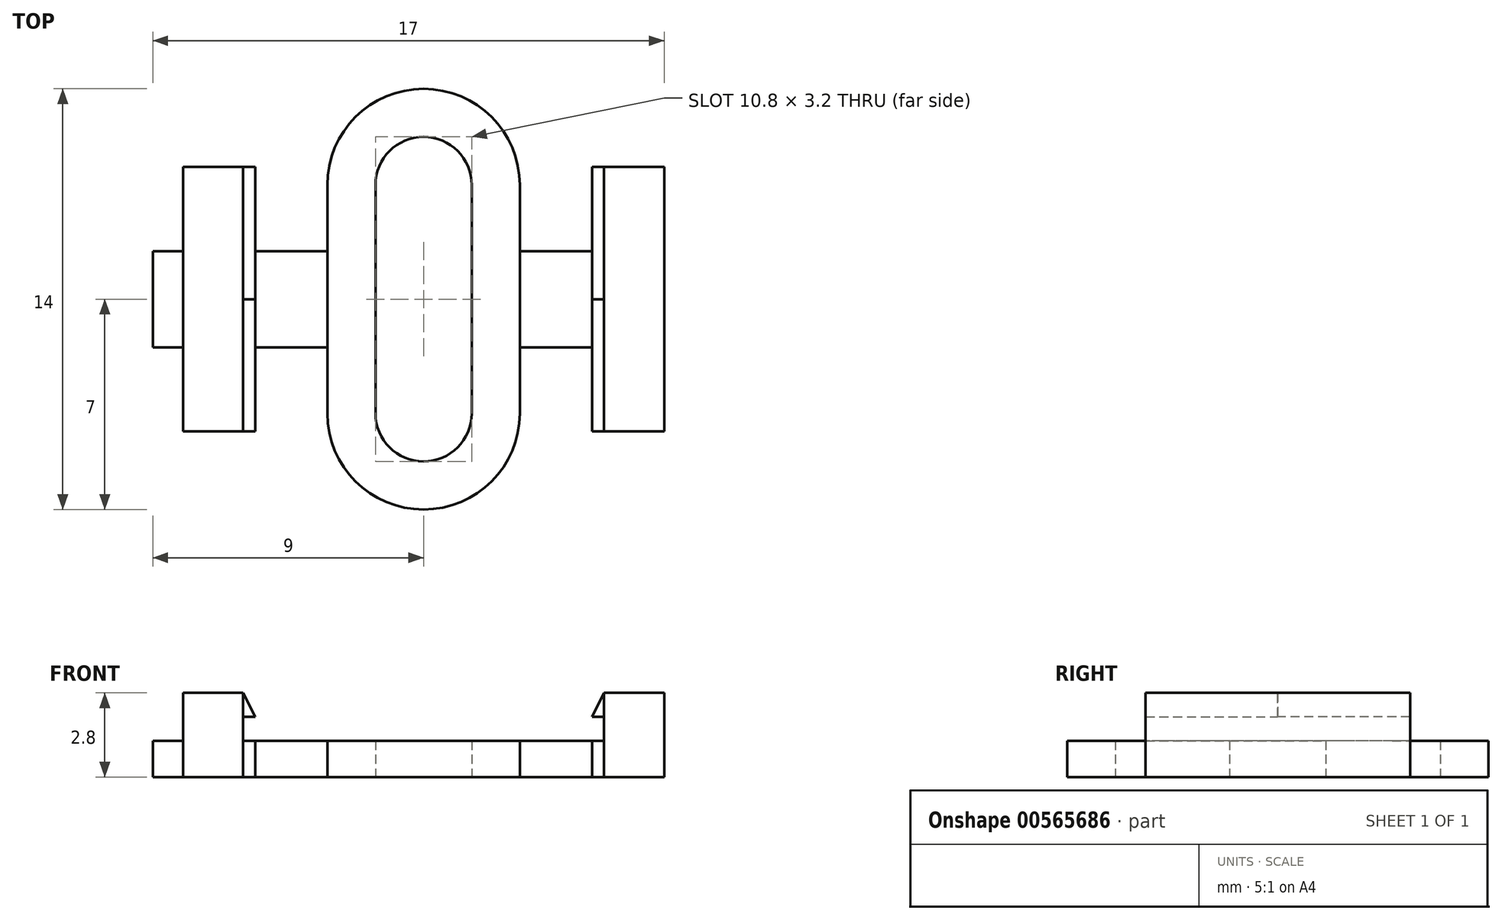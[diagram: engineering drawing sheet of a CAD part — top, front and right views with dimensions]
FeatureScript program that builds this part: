
annotation { "Feature Type Name" : "Feature", "Feature Type Description" : "" }
export const myFeature = defineFeature(function(context is Context, id is Id, definition is map)
    precondition{}
    {
        {
            var Q0;
            Q0=qCreatedBy(makeId("Top.planeOp"),FACE);
            var sketch = newSketch(context, id + "F0", { "sketchPlane" : qUnion([Q0])});
            skPoint(sketch, "E0", {"position": v(0, 4.4) * mm});
            skPoint(sketch, "E1", {"position": v(-8, 4.4) * mm});
            skPoint(sketch, "E2", {"position": v(-5.6, 4.4) * mm});
            skPoint(sketch, "E3", {"position": v(0, 1.6) * mm});
            skLineSegment(sketch, "E4", {"start": v(-8, 4.4) * mm, "end": v(-8, 0) * mm});
            skLineSegment(sketch, "E5", {"start": v(-8, 4.4) * mm, "end": v(-5.6, 4.4) * mm});
            skLineSegment(sketch, "E6", {"start": v(-5.6, 4.4) * mm, "end": v(-5.6, 1.6) * mm});
            skLineSegment(sketch, "E7", {"start": v(-5.6, 1.6) * mm, "end": v(-3.2, 1.6) * mm});
            skLineSegment(sketch, "E8", {"start": v(-3.2, 1.6) * mm, "end": v(-3.2, 3.8) * mm});
            skLineSegment(sketch, "E9", {"start": v(0, 7) * mm, "end": v(0, 7) * mm});
            skPoint(sketch, "E10", {"position": v(-1.6, 1.6) * mm});
            skPoint(sketch, "E11", {"position": v(-1.6, 5.4) * mm});
            skLineSegment(sketch, "E12", {"start": v(-1.6, 0) * mm, "end": v(-1.6, 3.8) * mm});
            skLineSegment(sketch, "E13", {"start": v(0, 5.4) * mm, "end": v(0, 5.4) * mm});
            skPoint(sketch, "E14.visualSharp", {"position": v(-3.2, 7) * mm});
            skArc(sketch, "E14.filletArc", {"start": v(0, 7) * mm, "mid": v(-2.26, 6.06) * mm, "end": v(-3.2, 3.8) * mm});
            skArc(sketch, "E15.filletArc", {"start": v(0, 5.4) * mm, "mid": v(-1.13, 4.93) * mm, "end": v(-1.6, 3.8) * mm});
            skPoint(sketch, "E16.MirrorP", {"position": v(1.6, 5.4) * mm});
            skLineSegment(sketch, "E17.MirrorCS", {"start": v(8, 4.4) * mm, "end": v(5.6, 4.4) * mm});
            skPoint(sketch, "E18.MirrorP", {"position": v(5.6, 4.4) * mm});
            skPoint(sketch, "E19.MirrorP", {"position": v(8, 4.4) * mm});
            skArc(sketch, "E20.MirrorCS", {"start": v(0, 5.4) * mm, "mid": v(1.13, 4.93) * mm, "end": v(1.6, 3.8) * mm});
            skLineSegment(sketch, "E21.MirrorCS", {"start": v(3.2, 1.6) * mm, "end": v(3.2, 3.8) * mm});
            skArc(sketch, "E22.MirrorCS", {"start": v(0, 7) * mm, "mid": v(2.26, 6.06) * mm, "end": v(3.2, 3.8) * mm});
            skLineSegment(sketch, "E23.MirrorCS", {"start": v(8, 4.4) * mm, "end": v(8, 0) * mm});
            skLineSegment(sketch, "E24.MirrorCS", {"start": v(1.6, 0) * mm, "end": v(1.6, 3.8) * mm});
            skLineSegment(sketch, "E25.MirrorCS", {"start": v(5.6, 4.4) * mm, "end": v(5.6, 1.6) * mm});
            skPoint(sketch, "E26.MirrorP", {"position": v(1.6, 1.6) * mm});
            skLineSegment(sketch, "E27.MirrorCS", {"start": v(5.6, 1.6) * mm, "end": v(3.2, 1.6) * mm});
            skPoint(sketch, "E28.MirrorP", {"position": v(3.2, 7) * mm});
            skLineSegment(sketch, "E29.MirrorCS", {"start": v(0, -5.4) * mm, "end": v(0, -5.4) * mm});
            skPoint(sketch, "E30.MirrorP", {"position": v(0, -4.4) * mm});
            skPoint(sketch, "E31.MirrorP", {"position": v(-1.6, -5.4) * mm});
            skLineSegment(sketch, "E32.MirrorCS", {"start": v(0, -7) * mm, "end": v(0, -7) * mm});
            skPoint(sketch, "E33.MirrorP", {"position": v(0, -1.6) * mm});
            skPoint(sketch, "E34.MirrorP", {"position": v(1.6, -5.4) * mm});
            skPoint(sketch, "E35.MirrorP", {"position": v(-1.6, -1.6) * mm});
            skPoint(sketch, "E36.MirrorP", {"position": v(1.6, -1.6) * mm});
            skLineSegment(sketch, "E37.MirrorCS", {"start": v(5.6, -1.6) * mm, "end": v(3.2, -1.6) * mm});
            skPoint(sketch, "E38.MirrorP", {"position": v(-8, -4.4) * mm});
            skLineSegment(sketch, "E39.MirrorCS", {"start": v(5.6, -4.4) * mm, "end": v(5.6, -1.6) * mm});
            skLineSegment(sketch, "E40.MirrorCS", {"start": v(-5.6, -4.4) * mm, "end": v(-5.6, -1.6) * mm});
            skLineSegment(sketch, "E41.MirrorCS", {"start": v(-5.6, -1.6) * mm, "end": v(-3.2, -1.6) * mm});
            skPoint(sketch, "E42.MirrorP", {"position": v(8, -4.4) * mm});
            skLineSegment(sketch, "E43.MirrorCS", {"start": v(-3.2, -1.6) * mm, "end": v(-3.2, -3.8) * mm});
            skLineSegment(sketch, "E44.MirrorCS", {"start": v(-1.6, 0) * mm, "end": v(-1.6, -3.8) * mm});
            skArc(sketch, "E45.MirrorCS", {"start": v(0, -5.4) * mm, "mid": v(-1.13, -4.93) * mm, "end": v(-1.6, -3.8) * mm});
            skLineSegment(sketch, "E46.MirrorCS", {"start": v(8, -4.4) * mm, "end": v(8, 0) * mm});
            skLineSegment(sketch, "E47.MirrorCS", {"start": v(3.2, -1.6) * mm, "end": v(3.2, -3.8) * mm});
            skArc(sketch, "E48.MirrorCS", {"start": v(0, -7) * mm, "mid": v(-2.26, -6.06) * mm, "end": v(-3.2, -3.8) * mm});
            skPoint(sketch, "E49.MirrorP", {"position": v(3.2, -7) * mm});
            skArc(sketch, "E50.MirrorCS", {"start": v(0, -5.4) * mm, "mid": v(1.13, -4.93) * mm, "end": v(1.6, -3.8) * mm});
            skPoint(sketch, "E51.MirrorP", {"position": v(-3.2, -7) * mm});
            skLineSegment(sketch, "E52.MirrorCS", {"start": v(-8, -4.4) * mm, "end": v(-8, 0) * mm});
            skPoint(sketch, "E53.MirrorP", {"position": v(-5.6, -4.4) * mm});
            skLineSegment(sketch, "E54.MirrorCS", {"start": v(-8, -4.4) * mm, "end": v(-5.6, -4.4) * mm});
            skLineSegment(sketch, "E55.MirrorCS", {"start": v(8, -4.4) * mm, "end": v(5.6, -4.4) * mm});
            skPoint(sketch, "E56.MirrorP", {"position": v(5.6, -4.4) * mm});
            skArc(sketch, "E57.MirrorCS", {"start": v(0, -7) * mm, "mid": v(2.26, -6.06) * mm, "end": v(3.2, -3.8) * mm});
            skLineSegment(sketch, "E58.MirrorCS", {"start": v(1.6, 0) * mm, "end": v(1.6, -3.8) * mm});
            skPoint(sketch, "E59", {"position": v(-6, 4.4) * mm});
            skLineSegment(sketch, "E60", {"start": v(-6, 4.4) * mm, "end": v(-6, -4.4) * mm});
            skPoint(sketch, "E61", {"position": v(6, 4.4) * mm});
            skLineSegment(sketch, "E62", {"start": v(6, 4.4) * mm, "end": v(6, -4.4) * mm});
            skLineSegment(sketch, "E63", {"start": v(-8, 1.6) * mm, "end": v(-9, 1.6) * mm});
            skLineSegment(sketch, "E64", {"start": v(-9, 1.6) * mm, "end": v(-9, -1.6) * mm});
            skLineSegment(sketch, "E65", {"start": v(-9, -1.6) * mm, "end": v(-8, -1.6) * mm});
            skLineSegment(sketch, "E66", {"start": v(-3.2, 1.6) * mm, "end": v(-3.2, -1.6) * mm});
            skLineSegment(sketch, "E67", {"start": v(3.2, -1.6) * mm, "end": v(3.2, 1.6) * mm});
            skSolve(sketch);
        }
        {
            var Q0;
            {var subQ4=sQuery(id+"F0.wireOp",EDGE,"E23.MirrorCS");Q0=makeQuery(id+"F0.imprint","IMPRINT",FACE,{"disambiguationData":[TD([[makeQuery(id+"F0.imprint","IMPRINT",EDGE,{"derivedFrom":subQ4}),-1.0]])]});}
            var Q1;
            {var subQ3=sQuery(id+"F0.wireOp",EDGE,"E4");Q1=makeQuery(id+"F0.imprint","IMPRINT",FACE,{"disambiguationData":[TD([[makeQuery(id+"F0.imprint","IMPRINT",EDGE,{"derivedFrom":subQ3}),1.0]])]});}
            extrude(context, id + "F1", {"entities" : qUnion([Q0, Q1]), "depth" : 2.8 * mm, "offsetDistance" : 25 * mm});
        }
        {
            var Q0;
            Q0=makeQuery(id+"F0.imprint","IMPRINT",FACE,{"disambiguationData":[TD([[makeQuery(id+"F0.imprint","IMPRINT",EDGE,{"derivedFrom":sQuery(id+"F0.wireOp",EDGE,"E14.filletArc")}),1.0]])]});
            extrude(context, id + "F2", {"entities" : qUnion([Q0]), "depth" : 1.2 * mm, "offsetDistance" : 25 * mm});
        }
        {
            var Q0;
            Q0=qCreatedBy(makeId("Front.planeOp"),FACE);
            var sketch = newSketch(context, id + "F3", { "sketchPlane" : qUnion([Q0])});
            skLineSegment(sketch, "E68", {"start": v(-6, 2.8) * mm, "end": v(-6, 2) * mm});
            skLineSegment(sketch, "E69", {"start": v(-6, 2) * mm, "end": v(-5.6, 2) * mm});
            skLineSegment(sketch, "E70", {"start": v(-5.6, 2) * mm, "end": v(-6, 2.8) * mm});
            skLineSegment(sketch, "E71", {"start": v(6, 2.8) * mm, "end": v(6, 2) * mm});
            skLineSegment(sketch, "E72", {"start": v(6, 2) * mm, "end": v(5.6, 2) * mm});
            skLineSegment(sketch, "E73", {"start": v(5.6, 2) * mm, "end": v(6, 2.8) * mm});
            skSolve(sketch);
        }
        {
            var Q0;
            Q0 = qSketchRegion(id + "F3", true);
            extrude(context, id + "F4", {"entities" : qUnion([Q0]), "depth" : 4.4 * mm, "offsetDistance" : 25 * mm});
        }
        {
            var Q0;
            Q0=makeQuery(id+"F4.opExtrude","CAP_FACE",FACE,{"disambiguationData":[OSD([sQuery(id+"F3.wireOp",EDGE,"E68"),sQuery(id+"F3.wireOp",EDGE,"E69"),sQuery(id+"F3.wireOp",EDGE,"E70")])],"isStart":true});
            var Q1;
            Q1=makeQuery(id+"F4.opExtrude","CAP_FACE",FACE,{"disambiguationData":[OSD([sQuery(id+"F3.wireOp",EDGE,"E71"),sQuery(id+"F3.wireOp",EDGE,"E72"),sQuery(id+"F3.wireOp",EDGE,"E73")])],"isStart":true});
            extrude(context, id + "F5", {"entities" : qUnion([Q0, Q1]), "depth" : 4.4 * mm, "offsetDistance" : 25 * mm});
        }
        {
            var Q0;
            {var subQ0=sQuery(id+"F0.wireOp",EDGE,"E63");Q0=makeQuery(id+"F0.imprint","IMPRINT",FACE,{"disambiguationData":[TD([[makeQuery(id+"F0.imprint","IMPRINT",EDGE,{"derivedFrom":subQ0}),1.0]])]});}
            extrude(context, id + "F6", {"entities" : qUnion([Q0]), "operationType" : NewBodyOperationType.ADD, "depth" : 1.2 * mm, "offsetDistance" : 25 * mm});
        }
        {
            var Q0;
            Q0=makeQuery(id+"F0.imprint","IMPRINT",FACE,{"disambiguationData":[TD([[makeQuery(id+"F0.imprint","IMPRINT",EDGE,{"derivedFrom":sQuery(id+"F0.wireOp",EDGE,"E27.MirrorCS")}),1.0]])]});
            var Q1;
            {var subQ2=sQuery(id+"F0.wireOp",EDGE,"E6");Q1=makeQuery(id+"F0.imprint","IMPRINT",FACE,{"disambiguationData":[TD([[makeQuery(id+"F0.imprint","IMPRINT",EDGE,{"derivedFrom":subQ2}),-1.0]])]});}
            extrude(context, id + "F7", {"entities" : qUnion([Q0, Q1]), "depth" : 1.2 * mm, "offsetDistance" : 25 * mm});
        }
    });
